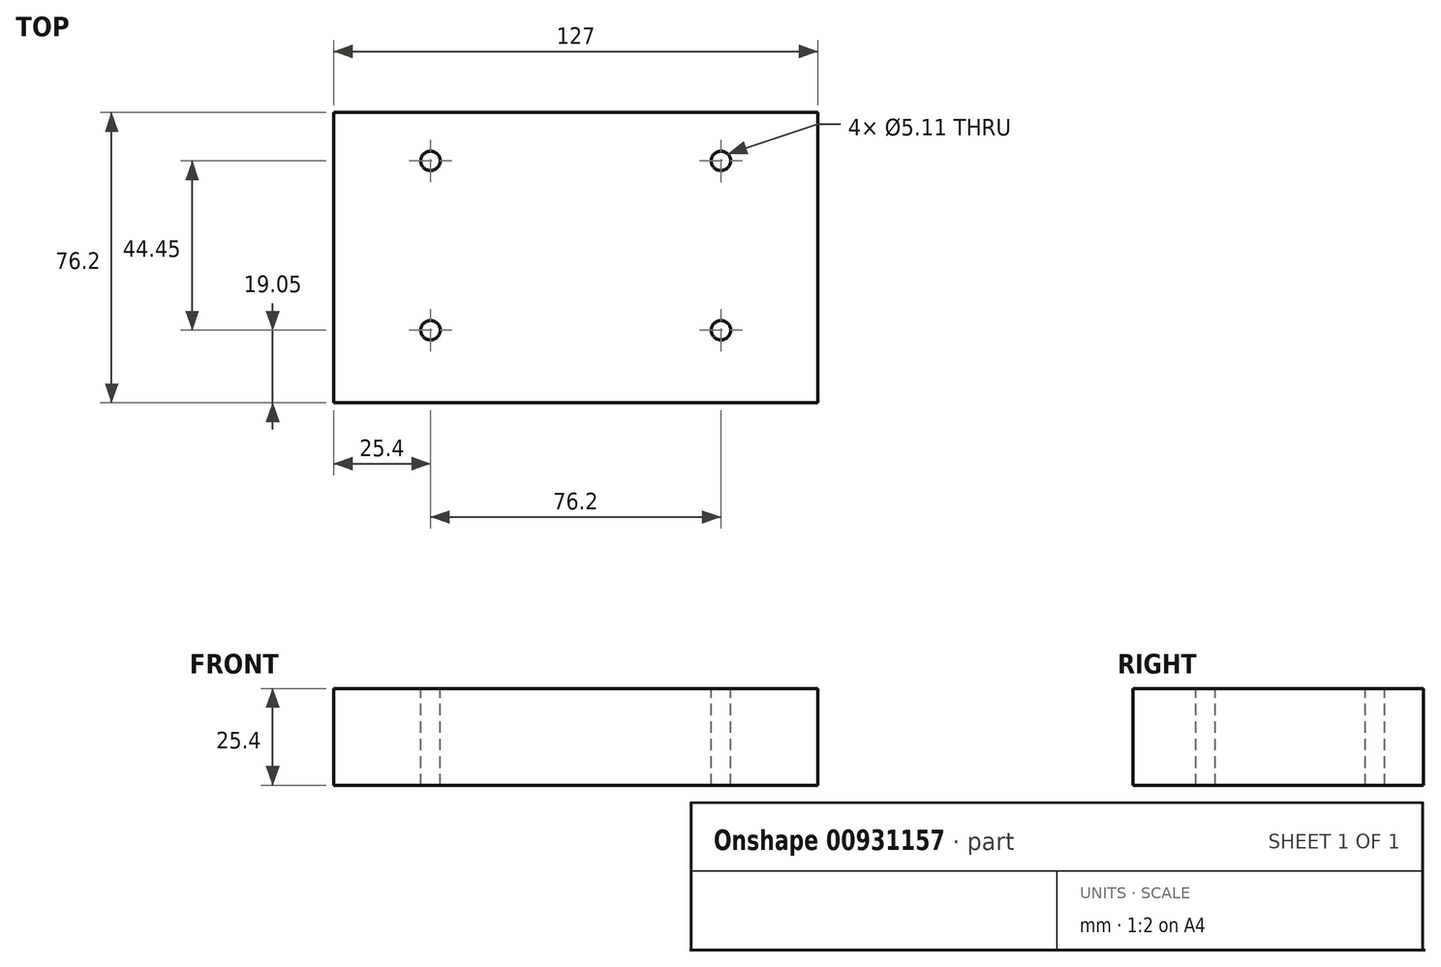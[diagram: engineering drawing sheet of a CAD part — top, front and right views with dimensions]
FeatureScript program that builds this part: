
annotation { "Feature Type Name" : "Feature", "Feature Type Description" : "" }
export const myFeature = defineFeature(function(context is Context, id is Id, definition is map)
    precondition{}
    {
        {
            var Q0;
            Q0=qCreatedBy(makeId("Top.planeOp"),FACE);
            var sketch = newSketch(context, id + "F0", { "sketchPlane" : qUnion([Q0])});
            skLineSegment(sketch, "E0.bottom", {"start": v(63.5, 38.1) * mm, "end": v(-63.5, 38.1) * mm});
            skLineSegment(sketch, "E0.top", {"start": v(63.5, -38.1) * mm, "end": v(-63.5, -38.1) * mm});
            skLineSegment(sketch, "E0.left", {"start": v(63.5, 38.1) * mm, "end": v(63.5, -38.1) * mm});
            skLineSegment(sketch, "E0.right", {"start": v(-63.5, 38.1) * mm, "end": v(-63.5, -38.1) * mm});
            skPoint(sketch, "E0.middle", {"position": v(0, 0) * mm});
            skSolve(sketch);
        }
        {
            var Q0;
            Q0 = qSketchRegion(id + "F0", true);
            var Q1;
            Q1=makeQuery(id+"F0.imprint","IMPRINT",FACE,{"disambiguationData":[TD([[makeQuery(id+"F0.imprint","IMPRINT",EDGE,{"derivedFrom":sQuery(id+"F0.wireOp",EDGE,"E0.bottom")}),1.0]])]});
            extrude(context, id + "F1", {"entities" : qUnion([Q0, Q1]), "depth" : 25.4 * mm, "offsetDistance" : 25.4 * mm});
        }
        {
            var Q0;
            Q0=makeQuery(id+"F1.opExtrude","CAP_FACE",FACE,{"disambiguationData":[OSD([sQuery(id+"F0.wireOp",EDGE,"E0.bottom"),sQuery(id+"F0.wireOp",EDGE,"E0.top"),sQuery(id+"F0.wireOp",EDGE,"E0.left"),sQuery(id+"F0.wireOp",EDGE,"E0.right")])],"isStart":false});
            var sketch = newSketch(context, id + "F2", { "sketchPlane" : qUnion([Q0])});
            skPoint(sketch, "E1", {"position": v(-38.1, -19.05) * mm});
            skPoint(sketch, "E2", {"position": v(-38.1, 25.4) * mm});
            skPoint(sketch, "E3", {"position": v(38.1, 25.4) * mm});
            skPoint(sketch, "E4", {"position": v(38.1, -19.05) * mm});
            skLineSegment(sketch, "E5", {"start": v(-44.92, 25.4) * mm, "end": v(51.52, 25.4) * mm, "construction": true});
            skLineSegment(sketch, "E6", {"start": v(-45.6, -19.05) * mm, "end": v(48.56, -19.05) * mm, "construction": true});
            skLineSegment(sketch, "E7", {"start": v(-38.1, 26.4) * mm, "end": v(-38.1, -29.56) * mm, "construction": true});
            skLineSegment(sketch, "E8", {"start": v(38.1, 27.53) * mm, "end": v(38.1, -27.97) * mm, "construction": true});
            skSolve(sketch);
        }
        {
            var Q0;
            Q0=sQuery(id+"F2.wireOp",VERTEX,"E2");
            var Q1;
            Q1=sQuery(id+"F2.wireOp",VERTEX,"E1");
            var Q2;
            Q2=sQuery(id+"F2.wireOp",VERTEX,"E3");
            var Q3;
            Q3=sQuery(id+"F2.wireOp",VERTEX,"E4");
            var Q4;
            Q4=makeQuery(id+"F1.opExtrude","SWEPT_BODY",BODY,{"disambiguationData":[OSD([sQuery(id+"F0.wireOp",EDGE,"E0.bottom"),sQuery(id+"F0.wireOp",EDGE,"E0.top"),sQuery(id+"F0.wireOp",EDGE,"E0.left"),sQuery(id+"F0.wireOp",EDGE,"E0.right")])]});
            hole(context, id + "F3", {"style" : HoleStyle.SIMPLE, "endStyle" : HoleEndStyle.THROUGH, "standardTappedOrClearance" : lookupTablePath({ "standard" : "ANSI", "engagement" : "75%", "pitch" : "20 tpi", "size" : "1/4", "type" : "Tapped" }), "standardBlindInLast" : lookupTablePath({ "standard" : "ANSI", "fit" : "Normal", "engagement" : "75%", "pitch" : "20 tpi", "size" : "1/4", "type" : "Clearance & tapped" }), "holeDiameter" : 5.1 * mm, "majorDiameter" : 6.35 * mm, "showTappedDepth" : true, "isTappedThrough" : true, "tappedDepth" : 12.7 * mm, "tapClearance" : 3, "locations" : qUnion([Q0, Q1, Q2, Q3]), "scope" : qUnion([Q4])});
        }
    });
